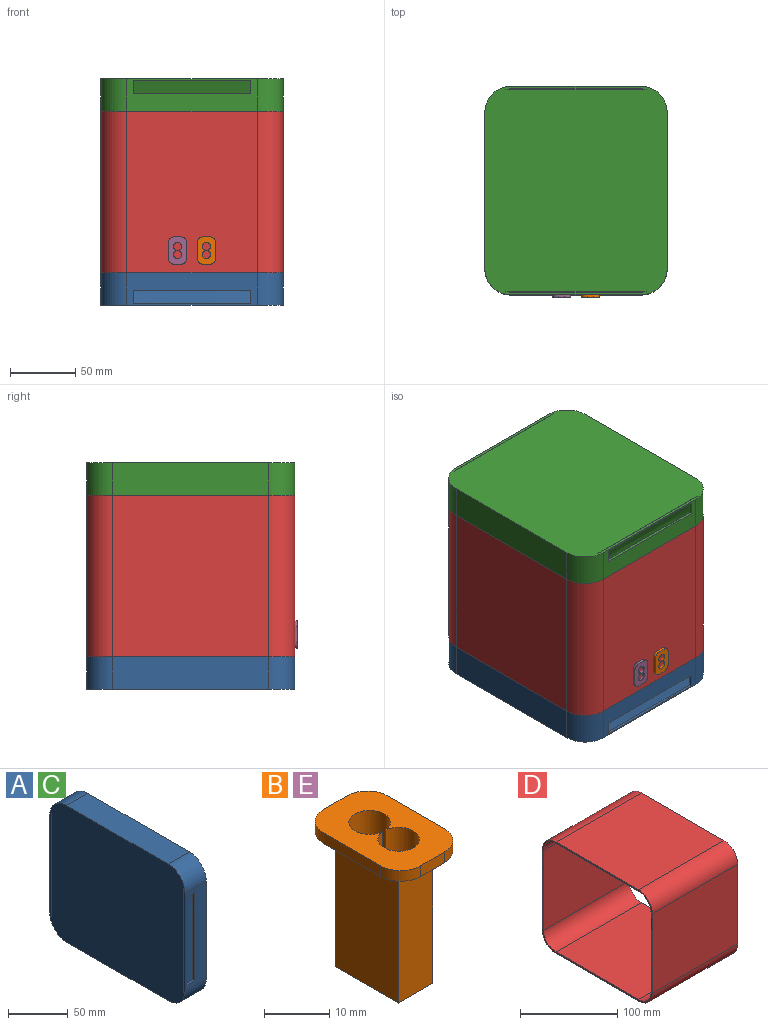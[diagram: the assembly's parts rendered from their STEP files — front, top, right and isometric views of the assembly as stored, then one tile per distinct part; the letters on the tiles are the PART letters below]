
ASSEMBLY  parts=5 mates=4
PART A: 41 faces, bbox 25.7x160x140 mm
  f0: bspline ~100x22.66mm, area 2286.8mm2, adj f1,f2,f15,f36
  f1: extruded ~22x13.42mm, area 240.4mm2, adj f0,f6,f15,f36
  f2: extruded ~22x13.42mm, area 240.4mm2, adj f0,f7,f15,f36
  f3: extruded ~22x13.42mm, area 240.4mm2, adj f5,f8,f15,f25
  f4: extruded ~22x13.42mm, area 240.4mm2, adj f5,f9,f15,f25
  f5: bspline ~100x22.66mm, area 2286.8mm2, adj f3,f4,f15,f25
  f6: cylinder r=18mm len=25mm, axis (1,0,0), area 599.6mm2, adj f1,f11,f12,f15,f17,f36,f39,f40
  f7: cylinder r=18mm len=25mm, axis (-1,0,0), area 599.6mm2, adj f2,f11,f12,f15,f16,f36,f38,f40
  f8: cylinder r=18mm len=25mm, axis (1,0,0), area 599.6mm2, adj f3,f10,f12,f15,f17,f25,f28,f40
  f9: cylinder r=18mm len=25mm, axis (-1,0,0), area 599.6mm2, adj f4,f10,f12,f15,f16,f25,f27,f40
  f10: plane 100x25mm, normal (0,-1,0), area 1600mm2, adj f8,f9,f15,f21,f22,f23,f24,f40
  f11: plane 100x25mm, normal (0,1,0), area 1600mm2, adj f6,f7,f15,f32,f33,f34,f35,f40
  f12: plane 150x136mm, normal (1,0,0), area 20256.8mm2, adj f6,f7,f8,f9,f16,f17,f26,f27
  f13: plane 120x25mm, normal (0,0,-1), area 3000mm2, adj f15,f19,f30,f40
  f14: plane 120x25mm, normal (0,0,1), area 3000mm2, adj f15,f20,f31,f40
  f15: plane 160x140mm, normal (-1,0,0), area 22004.9mm2, adj f0,f1,f2,f3,f4,f5,f6,f7
  f16: plane 120x23mm, normal (0,0,1), area 2760mm2, adj f7,f9,f12,f40
  f17: plane 120x23mm, normal (0,0,-1), area 2760mm2, adj f6,f8,f12,f40
  f18: plane 100x25mm, normal (0,1,0), area 1600mm2, adj f15,f19,f20,f21,f22,f23,f24,f40
  f19: cylinder r=20mm len=25mm, axis (-1,0,0), area 785.4mm2, adj f13,f15,f18,f40
  f20: cylinder r=20mm len=25mm, axis (1,0,0), area 785.4mm2, adj f14,f15,f18,f40
  f21: plane 90x2mm, normal (-1,0,0), area 180mm2, adj f10,f18,f22,f24
  f22: plane 10x2mm, normal (0,0,1), area 20mm2, adj f10,f18,f21,f23
  f23: plane 90x2mm, normal (1,0,0), area 180mm2, adj f10,f18,f22,f24
  f24: plane 10x2mm, normal (0,0,-1), area 20mm2, adj f10,f18,f21,f23
  f25: plane 129.93x2mm, normal (1,0,0), area 256.9mm2, adj f3,f4,f5,f8,f9,f26,f27,f28
  f26: bspline ~100x20mm, area 2073.2mm2, adj f12,f25,f27,f28
  f27: extruded ~20x14.97mm, area 276.3mm2, adj f9,f12,f25,f26
  f28: extruded ~20x14.97mm, area 276.3mm2, adj f8,f12,f25,f26
  f29: plane 100x25mm, normal (0,-1,0), area 1600mm2, adj f15,f30,f31,f32,f33,f34,f35,f40
  f30: cylinder r=20mm len=25mm, axis (-1,0,0), area 785.4mm2, adj f13,f15,f29,f40
  f31: cylinder r=20mm len=25mm, axis (1,0,0), area 785.4mm2, adj f14,f15,f29,f40
  f32: plane 90x2mm, normal (-1,0,0), area 180mm2, adj f11,f29,f33,f35
  f33: plane 10x2mm, normal (0,0,1), area 20mm2, adj f11,f29,f32,f34
  f34: plane 90x2mm, normal (1,0,0), area 180mm2, adj f11,f29,f33,f35
  f35: plane 10x2mm, normal (0,0,-1), area 20mm2, adj f11,f29,f32,f34
  f36: plane 129.93x2mm, normal (1,0,0), area 256.9mm2, adj f0,f1,f2,f6,f7,f37,f38,f39
  f37: bspline ~100x20mm, area 2073.2mm2, adj f12,f36,f38,f39
  f38: extruded ~20x14.97mm, area 276.3mm2, adj f7,f12,f36,f37
  f39: extruded ~20x14.97mm, area 276.3mm2, adj f6,f12,f36,f37
  f40: plane 160x140mm, normal (1,0,0), area 1118.8mm2, adj f6,f7,f8,f9,f10,f11,f13,f14
PART B: 17 faces, bbox 13.9x21.1x27 mm
  f0: plane 21.06x13.87mm, normal (0,0,-1), area 174.9mm2, adj f2,f3,f4,f5,f8,f9,f10,f11
  f1: cylinder r=3.17mm len=27mm, axis (0,0,-1), area 517.1mm2, adj f6,f7,f16
  f2: plane 12.37x2mm, normal (1,0,0), area 24.7mm2, adj f0,f7,f8,f11
  f3: plane 5.18x2mm, normal (0,1,0), area 10.4mm2, adj f0,f7,f8,f9
  f4: plane 12.37x2mm, normal (-1,0,0), area 24.7mm2, adj f0,f7,f9,f10
  f5: plane 5.18x2mm, normal (0,-1,0), area 10.4mm2, adj f0,f7,f10,f11
  f6: cylinder r=3.17mm len=27mm, axis (0,0,-1), area 517.1mm2, adj f1,f7,f16
  f7: plane 21.06x13.87mm, normal (0,0,1), area 212.6mm2, adj f1,f2,f3,f4,f5,f6,f8,f9
  f8: cylinder r=4.35mm len=4.35mm, axis (0,0,1), area 13.7mm2, adj f0,f2,f3,f7
  f9: cylinder r=4.35mm len=4.35mm, axis (0,0,-1), area 13.7mm2, adj f0,f3,f4,f7
  f10: cylinder r=4.35mm len=4.35mm, axis (0,0,1), area 13.7mm2, adj f0,f4,f5,f7
  f11: cylinder r=4.35mm len=4.35mm, axis (0,0,-1), area 13.7mm2, adj f0,f2,f5,f7
  f12: plane 25x7.41mm, normal (0,-1,0), area 185.2mm2, adj f0,f13,f15,f16
  f13: plane 25x13.64mm, normal (1,0,0), area 341mm2, adj f0,f12,f14,f16
  f14: plane 25x7.41mm, normal (0,1,0), area 185.2mm2, adj f0,f13,f15,f16
  f15: plane 25x13.64mm, normal (-1,0,0), area 341mm2, adj f0,f12,f14,f16
  f16: plane 13.64x7.41mm, normal (0,0,-1), area 37.8mm2, adj f1,f6,f12,f13,f14,f15
PART C: same geometry as A
PART D: 18 faces, bbox 124x160x140 mm
  f0: plane 160x140mm, normal (-1,0,0), area 1118.8mm2, adj f1,f2,f3,f4,f5,f6,f7,f8
  f1: cylinder r=20mm len=124mm, axis (1,0,0), area 3895.6mm2, adj f0,f3,f7,f9
  f2: cylinder r=20mm len=124mm, axis (-1,0,0), area 3895.6mm2, adj f0,f3,f8,f9
  f3: plane 124x100mm, normal (0,-1,0), area 12400mm2, adj f0,f1,f2,f9
  f4: cylinder r=20mm len=124mm, axis (-1,0,0), area 3895.6mm2, adj f0,f6,f8,f9
  f5: cylinder r=20mm len=124mm, axis (1,0,0), area 3895.6mm2, adj f0,f6,f7,f9
  f6: plane 124x100mm, normal (0,1,0), area 12400mm2, adj f0,f4,f5,f9
  f7: plane 124x120mm, normal (0,0,1), area 14880mm2, adj f0,f1,f5,f9
  f8: plane 124x120mm, normal (0,0,-1), area 14880mm2, adj f0,f2,f4,f9
  f9: plane 160x140mm, normal (1,0,0), area 1118.8mm2, adj f1,f2,f3,f4,f5,f6,f7,f8
  f10: cylinder r=18mm len=124mm, axis (-1,0,0), area 3506mm2, adj f0,f9,f12,f17
  f11: cylinder r=18mm len=124mm, axis (-1,0,0), area 3506mm2, adj f0,f9,f12,f16
  f12: plane 124x120mm, normal (0,0,1), area 14880mm2, adj f0,f9,f10,f11
  f13: cylinder r=18mm len=124mm, axis (1,0,0), area 3506mm2, adj f0,f9,f15,f17
  f14: cylinder r=18mm len=124mm, axis (1,0,0), area 3506mm2, adj f0,f9,f15,f16
  f15: plane 124x120mm, normal (0,0,-1), area 14880mm2, adj f0,f9,f13,f14
  f16: plane 124x100mm, normal (0,-1,0), area 12400mm2, adj f0,f9,f11,f14
  f17: plane 124x100mm, normal (0,1,0), area 12400mm2, adj f0,f9,f10,f13
PART E: same geometry as B
PLACE A rot(axis=(0.71,0,0.71),180deg) t=(-35.33,1.77,-137.98)mm
PLACE B rot(axis=(0,-0.71,0.71),180deg) t=(-78.6,-78.23,-137.17)mm
PLACE C rot(axis=(0,1,0),90deg) t=(-35.33,1.77,38.02)mm
PLACE D rot(axis=(0,1,0),90deg) t=(-35.33,1.77,38.02)mm
PLACE E rot(axis=(0,-0.71,0.71),180deg) t=(-100.71,-78.23,-137.17)mm
MATE fastened E.f0 <-> B.f0  axis (0,-1,0) through (-46.38,-78.23,-94.98)mm
MATE fastened A.f16 <-> D.f12  axis (1,0,0) through (-103.33,1.77,-111.98)mm
MATE fastened C.f16 <-> D.f12  axis (1,0,0) through (-103.33,1.77,12.02)mm
MATE fastened B.f0 <-> D.f3  axis (0,-1,0) through (-24.27,-78.23,-94.98)mm
